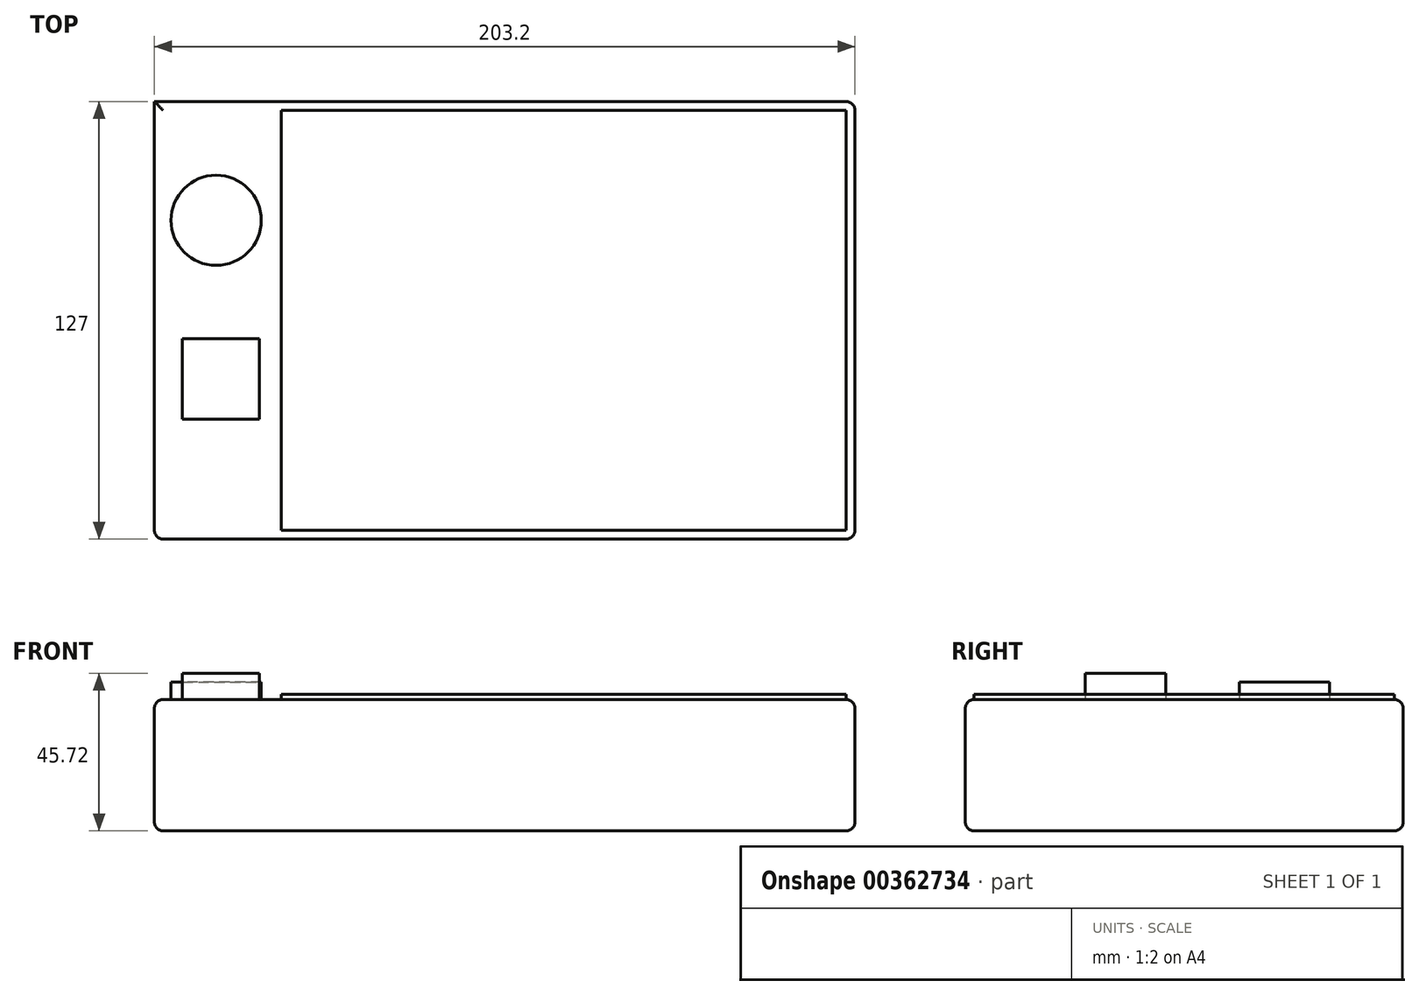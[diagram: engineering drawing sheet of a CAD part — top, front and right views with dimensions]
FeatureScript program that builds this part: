
annotation { "Feature Type Name" : "Feature", "Feature Type Description" : "" }
export const myFeature = defineFeature(function(context is Context, id is Id, definition is map)
    precondition{}
    {
        {
            var Q0;
            Q0=qCreatedBy(makeId("Top.planeOp"),FACE);
            var sketch = newSketch(context, id + "F0", { "sketchPlane" : qUnion([Q0])});
            skLineSegment(sketch, "E0.bottom", {"start": v(-107.64, -51.07) * mm, "end": v(95.56, -51.07) * mm});
            skLineSegment(sketch, "E0.top", {"start": v(-107.64, 75.93) * mm, "end": v(95.56, 75.93) * mm});
            skLineSegment(sketch, "E0.left", {"start": v(-107.64, -51.07) * mm, "end": v(-107.64, 75.93) * mm});
            skLineSegment(sketch, "E0.right", {"start": v(95.56, -51.07) * mm, "end": v(95.56, 75.93) * mm});
            skSolve(sketch);
        }
        {
            var Q0;
            Q0=makeQuery(id+"F0.imprint","IMPRINT",FACE,{"disambiguationData":[TD([[makeQuery(id+"F0.imprint","IMPRINT",EDGE,{"derivedFrom":sQuery(id+"F0.wireOp",EDGE,"E0.bottom")}),1.0]])]});
            extrude(context, id + "F1", {"entities" : qUnion([Q0]), "depth" : 38.1 * mm});
        }
        {
            var Q0;
            Q0=makeQuery(id+"F1.opExtrude","CAP_EDGE",EDGE,{"disambiguationData":[OSD([sQuery(id+"F0.wireOp",EDGE,"E0.bottom")])],"isStart":true});
            var Q1;
            Q1=makeQuery(id+"F1.opExtrude","CAP_EDGE",EDGE,{"disambiguationData":[OSD([sQuery(id+"F0.wireOp",EDGE,"E0.bottom")])],"isStart":false});
            var Q2;
            Q2=makeQuery(id+"F1.opExtrude","SWEPT_FACE",FACE,{"disambiguationData":[OSD([sQuery(id+"F0.wireOp",EDGE,"E0.bottom")])]});
            var Q3;
            Q3=makeQuery(id+"F1.opExtrude","CAP_EDGE",EDGE,{"disambiguationData":[OSD([sQuery(id+"F0.wireOp",EDGE,"E0.right")])],"isStart":false});
            var Q4;
            Q4=makeQuery(id+"F1.opExtrude","CAP_EDGE",EDGE,{"disambiguationData":[OSD([sQuery(id+"F0.wireOp",EDGE,"E0.right")])],"isStart":true});
            var Q5;
            Q5=makeQuery(id+"F1.opExtrude","SWEPT_EDGE",EDGE,{"disambiguationData":[OSD([sQuery(id+"F0.wireOp",EDGE,"E0.top"),sQuery(id+"F0.wireOp",EDGE,"E0.right")])]});
            var Q6;
            Q6=makeQuery(id+"F1.opExtrude","CAP_EDGE",EDGE,{"disambiguationData":[OSD([sQuery(id+"F0.wireOp",EDGE,"E0.top")])],"isStart":false});
            var Q7;
            Q7=makeQuery(id+"F1.opExtrude","CAP_EDGE",EDGE,{"disambiguationData":[OSD([sQuery(id+"F0.wireOp",EDGE,"E0.left")])],"isStart":false});
            var Q8;
            Q8=makeQuery(id+"F1.opExtrude","CAP_EDGE",EDGE,{"disambiguationData":[OSD([sQuery(id+"F0.wireOp",EDGE,"E0.top")])],"isStart":true});
            var Q9;
            Q9=makeQuery(id+"F1.opExtrude","CAP_FACE",FACE,{"disambiguationData":[OSD([sQuery(id+"F0.wireOp",EDGE,"E0.bottom"),sQuery(id+"F0.wireOp",EDGE,"E0.top"),sQuery(id+"F0.wireOp",EDGE,"E0.left"),sQuery(id+"F0.wireOp",EDGE,"E0.right")])],"isStart":true});
            var Q10;
            Q10=makeQuery(id+"F1.opExtrude","CAP_EDGE",EDGE,{"disambiguationData":[OSD([sQuery(id+"F0.wireOp",EDGE,"E0.left")])],"isStart":true});
            fillet(context, id + "F2", {"entities" : qUnion([Q0, Q1, Q2, Q3, Q4, Q5, Q6, Q7, Q8, Q9, Q10]), "radius" : 2.54 * mm, "tangentPropagation" : true, "allowEdgeOverflow" : false});
        }
        {
            var Q0;
            Q0=makeQuery(id+"F1.opExtrude","CAP_FACE",FACE,{"disambiguationData":[OSD([sQuery(id+"F0.wireOp",EDGE,"E0.bottom"),sQuery(id+"F0.wireOp",EDGE,"E0.top"),sQuery(id+"F0.wireOp",EDGE,"E0.left"),sQuery(id+"F0.wireOp",EDGE,"E0.right")])],"isStart":false});
            var sketch = newSketch(context, id + "F3", { "sketchPlane" : qUnion([Q0])});
            skCircle(sketch, "E1", {"center": v(-89.75, 41.45) * mm, "radius": 13.09 * mm});
            skCircle(sketch, "E2", {"center": v(-147.07, 16.03) * mm, "radius": 7.09 * mm});
            skSolve(sketch);
        }
        {
            var Q0;
            Q0=makeQuery(id+"F3.imprint","IMPRINT",FACE,{"disambiguationData":[TD([[makeQuery(id+"F3.imprint","IMPRINT",EDGE,{"derivedFrom":sQuery(id+"F3.wireOp",EDGE,"E1")}),1.0]])]});
            extrude(context, id + "F4", {"entities" : qUnion([Q0]), "operationType" : NewBodyOperationType.ADD, "depth" : 5.08 * mm});
        }
        {
            var Q0;
            Q0=makeQuery(id+"F1.opExtrude","CAP_FACE",FACE,{"disambiguationData":[OSD([sQuery(id+"F0.wireOp",EDGE,"E0.bottom"),sQuery(id+"F0.wireOp",EDGE,"E0.top"),sQuery(id+"F0.wireOp",EDGE,"E0.left"),sQuery(id+"F0.wireOp",EDGE,"E0.right")])],"isStart":false});
            var sketch = newSketch(context, id + "F5", { "sketchPlane" : qUnion([Q0])});
            skLineSegment(sketch, "E3.bottom", {"start": v(-99.49, -16.23) * mm, "end": v(-77.17, -16.23) * mm});
            skLineSegment(sketch, "E3.top", {"start": v(-99.49, 7.03) * mm, "end": v(-77.17, 7.03) * mm});
            skLineSegment(sketch, "E3.left", {"start": v(-99.49, -16.23) * mm, "end": v(-99.49, 7.03) * mm});
            skLineSegment(sketch, "E3.right", {"start": v(-77.17, -16.23) * mm, "end": v(-77.17, 7.03) * mm});
            skSolve(sketch);
        }
        {
            var Q0;
            Q0=makeQuery(id+"F5.imprint","IMPRINT",FACE,{"disambiguationData":[TD([[makeQuery(id+"F5.imprint","IMPRINT",EDGE,{"derivedFrom":sQuery(id+"F5.wireOp",EDGE,"E3.bottom")}),1.0]])]});
            extrude(context, id + "F6", {"entities" : qUnion([Q0]), "operationType" : NewBodyOperationType.ADD, "depth" : 7.62 * mm});
        }
        {
            var Q0;
            Q0=makeQuery(id+"F1.opExtrude","CAP_FACE",FACE,{"disambiguationData":[OSD([sQuery(id+"F0.wireOp",EDGE,"E0.bottom"),sQuery(id+"F0.wireOp",EDGE,"E0.top"),sQuery(id+"F0.wireOp",EDGE,"E0.left"),sQuery(id+"F0.wireOp",EDGE,"E0.right")])],"isStart":false});
            var sketch = newSketch(context, id + "F7", { "sketchPlane" : qUnion([Q0])});
            skLineSegment(sketch, "E4.bottom", {"start": v(-70.9, -48.53) * mm, "end": v(93.02, -48.53) * mm});
            skLineSegment(sketch, "E4.top", {"start": v(-70.9, 73.4) * mm, "end": v(93.02, 73.4) * mm});
            skLineSegment(sketch, "E4.left", {"start": v(-70.9, -48.53) * mm, "end": v(-70.9, 73.4) * mm});
            skLineSegment(sketch, "E4.right", {"start": v(93.02, -48.53) * mm, "end": v(93.02, 73.4) * mm});
            skSolve(sketch);
        }
        {
            var Q0;
            Q0=makeQuery(id+"F7.imprint","IMPRINT",FACE,{"disambiguationData":[TD([[makeQuery(id+"F7.imprint","IMPRINT",EDGE,{"derivedFrom":sQuery(id+"F7.wireOp",EDGE,"E4.bottom")}),1.0]])]});
            extrude(context, id + "F8", {"entities" : qUnion([Q0]), "operationType" : NewBodyOperationType.ADD, "depth" : 1.52 * mm});
        }
    });
